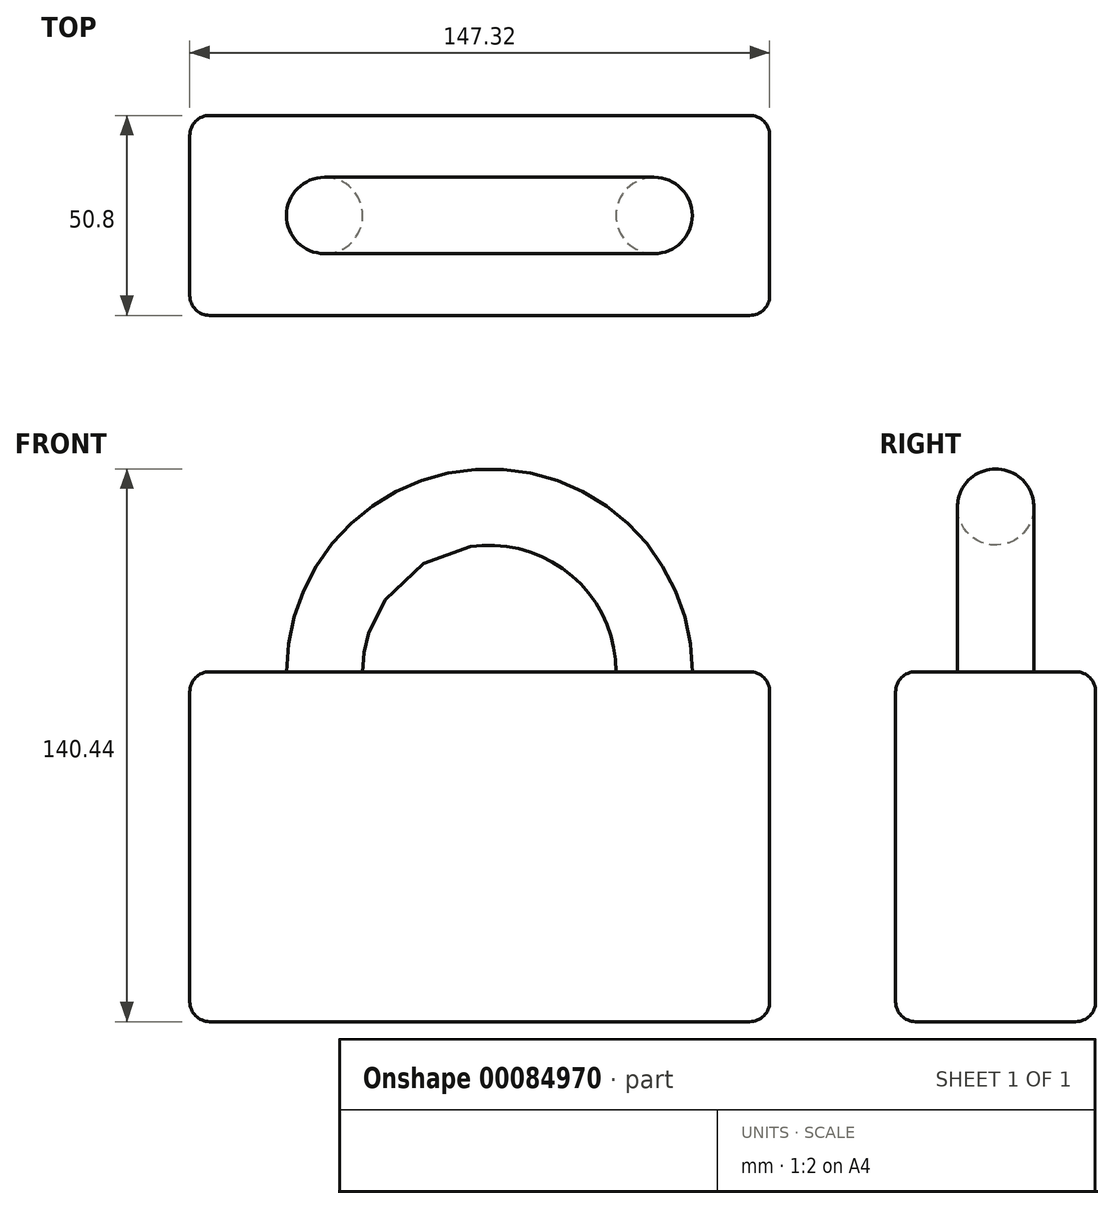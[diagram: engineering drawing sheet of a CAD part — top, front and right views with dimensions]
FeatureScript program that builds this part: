
annotation { "Feature Type Name" : "Feature", "Feature Type Description" : "" }
export const myFeature = defineFeature(function(context is Context, id is Id, definition is map)
    precondition{}
    {
        {
            var Q0;
            Q0=qCreatedBy(makeId("Front.planeOp"),FACE);
            var sketch = newSketch(context, id + "F0", { "sketchPlane" : qUnion([Q0])});
            skPoint(sketch, "E0", {"position": v(-9.68, -37.58) * mm});
            skLineSegment(sketch, "E1", {"start": v(37.58, -37.58) * mm, "end": v(37.58, 0) * mm});
            skLineSegment(sketch, "E2", {"start": v(-46.13, -37.58) * mm, "end": v(-46.13, 0) * mm});
            skArc(sketch, "E3", {"start": v(37.58, 0) * mm, "mid": v(-4.27, 41.86) * mm, "end": v(-46.13, 0) * mm});
            skSolve(sketch);
        }
        {
            var Q0;
            Q0=qCreatedBy(makeId("Top.planeOp"),FACE);
            var sketch = newSketch(context, id + "F1", { "sketchPlane" : qUnion([Q0])});
            skCircle(sketch, "E4", {"center": v(37.58, 0) * mm, "radius": 9.69 * mm});
            skSolve(sketch);
        }
        {
            var Q0;
            Q0=makeQuery(id+"F1.imprint","IMPRINT",FACE,{"disambiguationData":[TD([[makeQuery(id+"F1.imprint","IMPRINT",EDGE,{"derivedFrom":sQuery(id+"F1.wireOp",EDGE,"E4")}),1.0]])]});
            var Q1;
            Q1=sQuery(id+"F0.wireOp",EDGE,"E3");
            sweep(context, id + "F2", {"profiles" : qUnion([Q0]), "path" : qUnion([Q1])});
        }
        {
            var Q0;
            Q0=qCreatedBy(makeId("Front.planeOp"),FACE);
            var sketch = newSketch(context, id + "F3", { "sketchPlane" : qUnion([Q0])});
            skLineSegment(sketch, "E5.bottom", {"start": v(-80.38, 0) * mm, "end": v(66.94, 0) * mm});
            skLineSegment(sketch, "E5.top", {"start": v(-80.38, -88.9) * mm, "end": v(66.94, -88.9) * mm});
            skLineSegment(sketch, "E5.left", {"start": v(-80.38, 0) * mm, "end": v(-80.38, -88.9) * mm});
            skLineSegment(sketch, "E5.right", {"start": v(66.94, 0) * mm, "end": v(66.94, -88.9) * mm});
            skSolve(sketch);
        }
        {
            var Q0;
            Q0=makeQuery(id+"F3.imprint","IMPRINT",FACE,{"disambiguationData":[TD([[makeQuery(id+"F3.imprint","IMPRINT",EDGE,{"derivedFrom":sQuery(id+"F3.wireOp",EDGE,"E5.bottom")}),-1.0]])]});
            extrude(context, id + "F4", {"entities" : qUnion([Q0]), "operationType" : NewBodyOperationType.ADD, "endBound" : BoundingType.SYMMETRIC, "depth" : 50.8 * mm});
        }
        {
            var Q0;
            Q0=makeQuery(id+"F4.opExtrude","CAP_EDGE",EDGE,{"disambiguationData":[OSD([sQuery(id+"F3.wireOp",EDGE,"E5.left")])],"isStart":false});
            var Q1;
            Q1=makeQuery(id+"F4.opExtrude","CAP_EDGE",EDGE,{"disambiguationData":[OSD([sQuery(id+"F3.wireOp",EDGE,"E5.right")])],"isStart":false});
            var Q2;
            Q2=makeQuery(id+"F4.opExtrude","CAP_EDGE",EDGE,{"disambiguationData":[OSD([sQuery(id+"F3.wireOp",EDGE,"E5.right")])],"isStart":true});
            var Q3;
            Q3=makeQuery(id+"F4.opExtrude","CAP_EDGE",EDGE,{"disambiguationData":[OSD([sQuery(id+"F3.wireOp",EDGE,"E5.left")])],"isStart":true});
            var Q4;
            Q4=makeQuery(id+"F4.opExtrude","CAP_EDGE",EDGE,{"disambiguationData":[OSD([sQuery(id+"F3.wireOp",EDGE,"E5.bottom")])],"isStart":true});
            var Q5;
            Q5=makeQuery(id+"F4.opExtrude","CAP_EDGE",EDGE,{"disambiguationData":[OSD([sQuery(id+"F3.wireOp",EDGE,"E5.top")])],"isStart":false});
            var Q6;
            Q6=makeQuery(id+"F4.opExtrude","CAP_EDGE",EDGE,{"disambiguationData":[OSD([sQuery(id+"F3.wireOp",EDGE,"E5.bottom")])],"isStart":false});
            fillet(context, id + "F5", {"entities" : qUnion([Q0, Q1, Q2, Q3, Q4, Q5, Q6]), "radius" : 5.08 * mm, "tangentPropagation" : true, "allowEdgeOverflow" : false});
        }
        {
            var Q0;
            Q0=makeQuery(id+"F4.opExtrude","SWEPT_EDGE",EDGE,{"disambiguationData":[OSD([sQuery(id+"F3.wireOp",EDGE,"E5.bottom"),sQuery(id+"F3.wireOp",EDGE,"E5.right")])]});
            fillet(context, id + "F6", {"entities" : qUnion([Q0]), "radius" : 5.08 * mm, "tangentPropagation" : true, "allowEdgeOverflow" : false});
        }
        {
            var Q0;
            Q0=makeQuery(id+"F4.opExtrude","SWEPT_EDGE",EDGE,{"disambiguationData":[OSD([sQuery(id+"F3.wireOp",EDGE,"E5.bottom"),sQuery(id+"F3.wireOp",EDGE,"E5.left")])]});
            fillet(context, id + "F7", {"entities" : qUnion([Q0]), "radius" : 5.08 * mm, "tangentPropagation" : true, "allowEdgeOverflow" : false});
        }
        {
            var Q0;
            Q0=makeQuery(id+"F4.opExtrude","SWEPT_EDGE",EDGE,{"disambiguationData":[OSD([sQuery(id+"F3.wireOp",EDGE,"E5.top"),sQuery(id+"F3.wireOp",EDGE,"E5.left")])]});
            fillet(context, id + "F8", {"entities" : qUnion([Q0]), "radius" : 5.08 * mm, "tangentPropagation" : true, "allowEdgeOverflow" : false});
        }
    });
